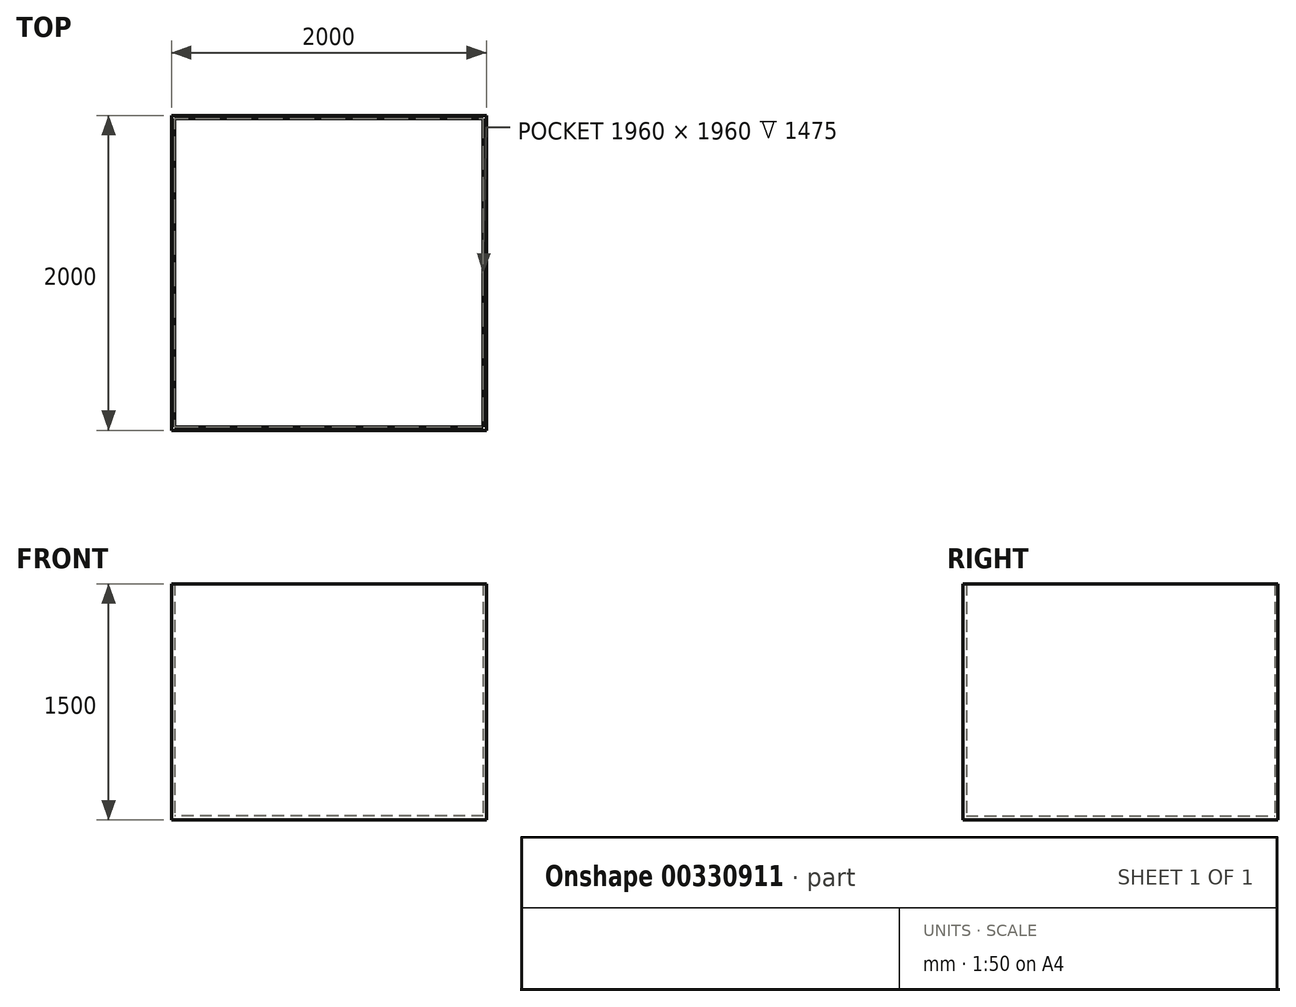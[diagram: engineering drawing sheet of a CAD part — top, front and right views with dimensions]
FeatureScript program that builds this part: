
annotation { "Feature Type Name" : "Feature", "Feature Type Description" : "" }
export const myFeature = defineFeature(function(context is Context, id is Id, definition is map)
    precondition{}
    {
        {
            var Q0;
            Q0=qCreatedBy(makeId("Top.planeOp"),FACE);
            var sketch = newSketch(context, id + "F0", { "sketchPlane" : qUnion([Q0])});
            skLineSegment(sketch, "E0.bottom", {"start": v(-1000, 1000) * mm, "end": v(1000, 1000) * mm});
            skLineSegment(sketch, "E0.top", {"start": v(-1000, -1000) * mm, "end": v(1000, -1000) * mm});
            skLineSegment(sketch, "E0.left", {"start": v(-1000, 1000) * mm, "end": v(-1000, -1000) * mm});
            skLineSegment(sketch, "E0.right", {"start": v(1000, 1000) * mm, "end": v(1000, -1000) * mm});
            skPoint(sketch, "E0.middle", {"position": v(0, 0) * mm});
            skLineSegment(sketch, "E1.0", {"start": v(980, 980) * mm, "end": v(980, -980) * mm});
            skLineSegment(sketch, "E1.1", {"start": v(-980, 980) * mm, "end": v(980, 980) * mm});
            skLineSegment(sketch, "E1.2", {"start": v(-980, 980) * mm, "end": v(-980, -980) * mm});
            skLineSegment(sketch, "E1.3", {"start": v(-980, -980) * mm, "end": v(980, -980) * mm});
            skSolve(sketch);
        }
        {
            var Q0;
            Q0 = qSketchRegion(id + "F0", true);
            extrude(context, id + "F1", {"entities" : qUnion([Q0]), "depth" : 1500 * mm});
        }
        {
            var Q0;
            Q0=makeQuery(id+"F1.opExtrude","CAP_FACE",FACE,{"disambiguationData":[OSD([sQuery(id+"F0.wireOp",EDGE,"E0.bottom"),sQuery(id+"F0.wireOp",EDGE,"E0.top"),sQuery(id+"F0.wireOp",EDGE,"E0.left"),sQuery(id+"F0.wireOp",EDGE,"E0.right"),sQuery(id+"F0.wireOp",EDGE,"E1.0"),sQuery(id+"F0.wireOp",EDGE,"E1.1"),sQuery(id+"F0.wireOp",EDGE,"E1.2"),sQuery(id+"F0.wireOp",EDGE,"E1.3")])],"isStart":true});
            var sketch = newSketch(context, id + "F2", { "sketchPlane" : qUnion([Q0])});
            skLineSegment(sketch, "E2.0", {"start": v(1000, -1000) * mm, "end": v(1000, 1000) * mm});
            skLineSegment(sketch, "E2.1", {"start": v(-1000, -1000) * mm, "end": v(-1000, 1000) * mm});
            skLineSegment(sketch, "E2.2", {"start": v(-1000, -1000) * mm, "end": v(1000, -1000) * mm});
            skLineSegment(sketch, "E2.3", {"start": v(-1000, 1000) * mm, "end": v(1000, 1000) * mm});
            skSolve(sketch);
        }
        {
            var Q0;
            Q0 = qSketchRegion(id + "F2", true);
            extrude(context, id + "F3", {"entities" : qUnion([Q0]), "operationType" : NewBodyOperationType.ADD, "oppositeDirection" : true, "depth" : 25 * mm});
        }
    });
